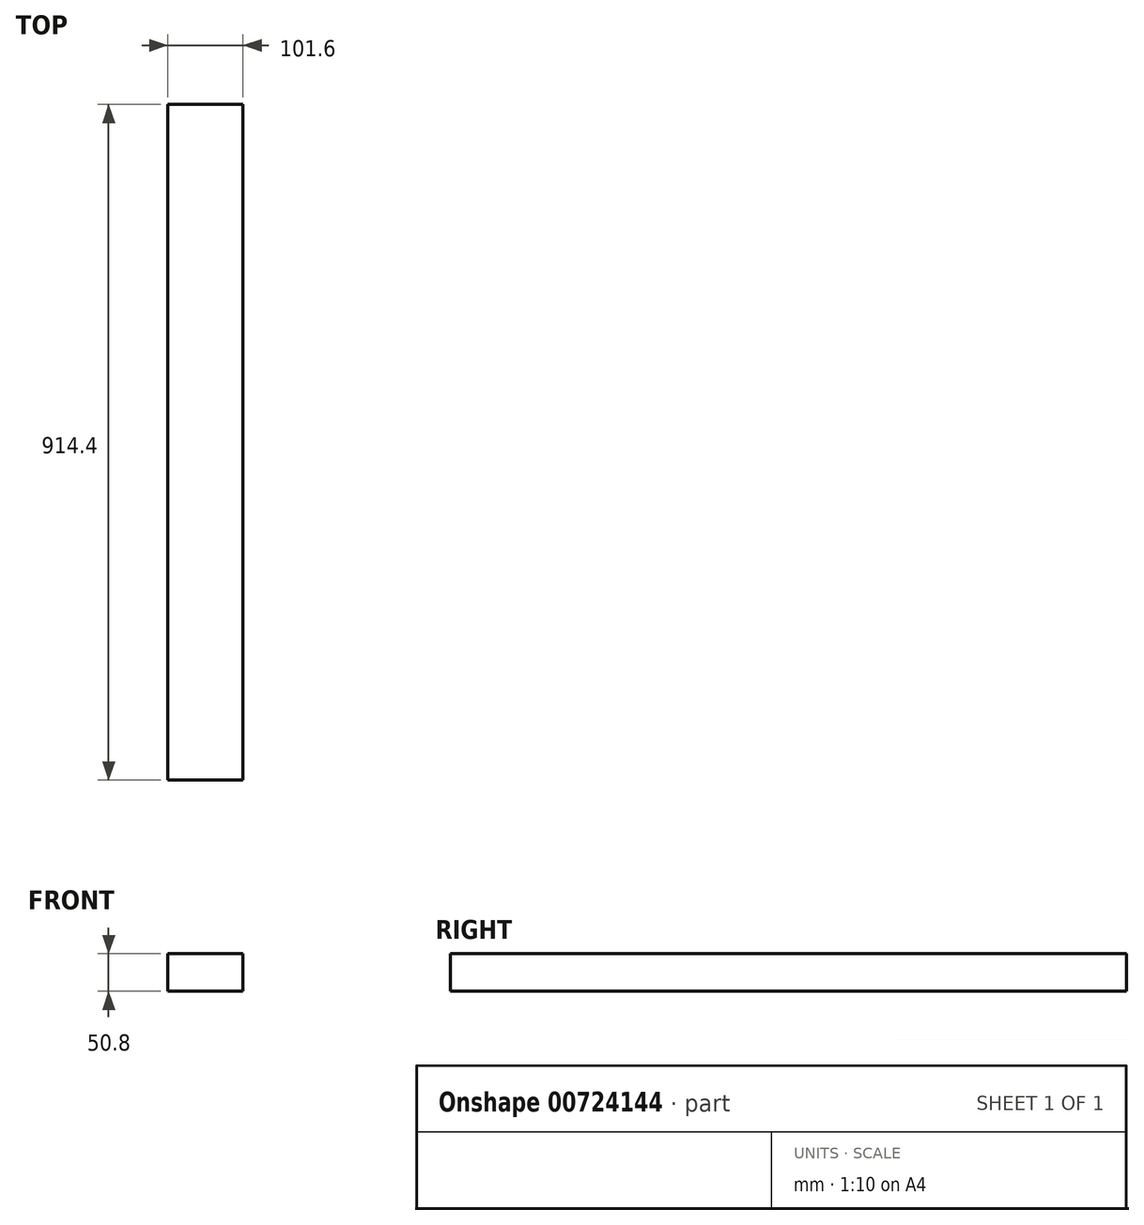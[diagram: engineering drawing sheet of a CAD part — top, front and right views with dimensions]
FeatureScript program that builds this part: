
annotation { "Feature Type Name" : "Feature", "Feature Type Description" : "" }
export const myFeature = defineFeature(function(context is Context, id is Id, definition is map)
    precondition{}
    {
        {
            var Q0;
            Q0=qCreatedBy(makeId("Top.planeOp"),FACE);
            var sketch = newSketch(context, id + "F0", { "sketchPlane" : qUnion([Q0])});
            skLineSegment(sketch, "E0.bottom", {"start": v(-292.07, 721.14) * mm, "end": v(-190.47, 721.14) * mm});
            skLineSegment(sketch, "E0.top", {"start": v(-292.07, -193.26) * mm, "end": v(-190.47, -193.26) * mm});
            skLineSegment(sketch, "E0.left", {"start": v(-292.07, 721.14) * mm, "end": v(-292.07, -193.26) * mm});
            skLineSegment(sketch, "E0.right", {"start": v(-190.47, 721.14) * mm, "end": v(-190.47, -193.26) * mm});
            skSolve(sketch);
        }
        {
            var Q0;
            Q0 = qSketchRegion(id + "F0", true);
            extrude(context, id + "F1", {"entities" : qUnion([Q0]), "depth" : 50.8 * mm, "offsetDistance" : 25.4 * mm});
        }
    });
